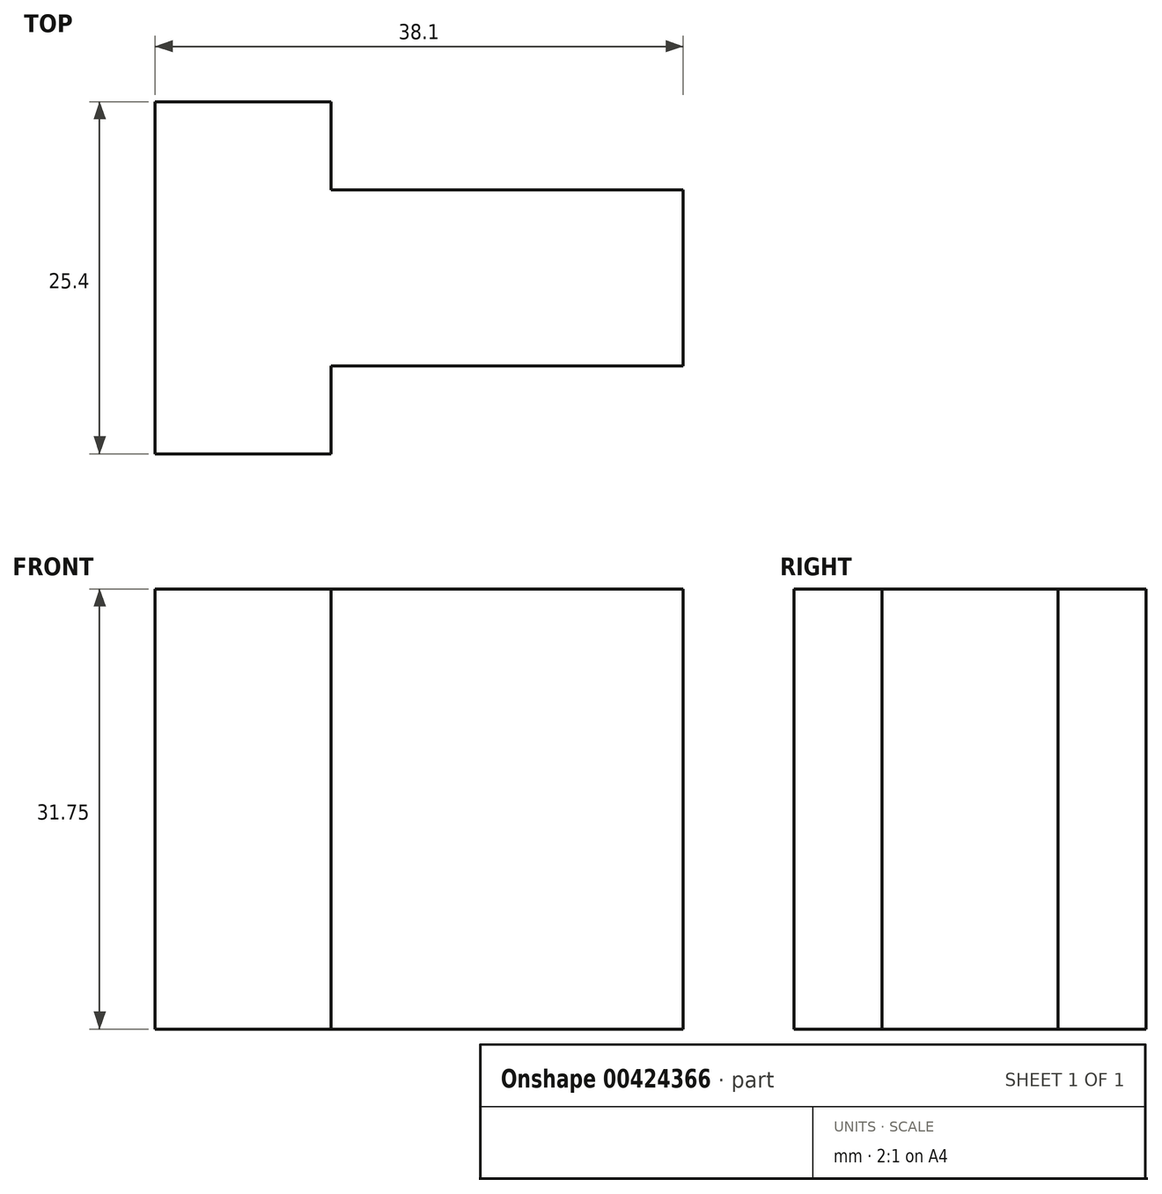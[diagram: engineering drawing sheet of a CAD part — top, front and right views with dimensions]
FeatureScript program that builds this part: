
annotation { "Feature Type Name" : "Feature", "Feature Type Description" : "" }
export const myFeature = defineFeature(function(context is Context, id is Id, definition is map)
    precondition{}
    {
        {
            var Q0;
            Q0=qCreatedBy(makeId("Top.planeOp"),FACE);
            var sketch = newSketch(context, id + "F0", { "sketchPlane" : qUnion([Q0])});
            skLineSegment(sketch, "E0", {"start": v(0, 0) * mm, "end": v(12.7, 0) * mm});
            skLineSegment(sketch, "E1", {"start": v(12.7, 0) * mm, "end": v(12.7, 6.35) * mm});
            skLineSegment(sketch, "E2", {"start": v(12.7, 6.35) * mm, "end": v(38.1, 6.35) * mm});
            skLineSegment(sketch, "E3", {"start": v(38.1, 6.35) * mm, "end": v(38.1, 19.05) * mm});
            skLineSegment(sketch, "E4", {"start": v(38.1, 19.05) * mm, "end": v(12.7, 19.05) * mm});
            skLineSegment(sketch, "E5", {"start": v(12.7, 19.05) * mm, "end": v(12.7, 25.4) * mm});
            skLineSegment(sketch, "E6", {"start": v(12.7, 25.4) * mm, "end": v(0, 25.4) * mm});
            skLineSegment(sketch, "E7", {"start": v(0, 25.4) * mm, "end": v(0, -1.56) * mm});
            skSolve(sketch);
        }
        {
            var Q0;
            {var subQ0=sQuery(id+"F0.wireOp",EDGE,"E0");Q0=makeQuery(id+"F0.imprint","IMPRINT",FACE,{"disambiguationData":[TD([[makeQuery(id+"F0.imprint","IMPRINT",EDGE,{"derivedFrom":subQ0}),1.0]])]});}
            extrude(context, id + "F1", {"entities" : qUnion([Q0]), "depth" : 31.75 * mm});
        }
    });
